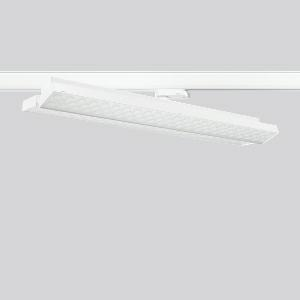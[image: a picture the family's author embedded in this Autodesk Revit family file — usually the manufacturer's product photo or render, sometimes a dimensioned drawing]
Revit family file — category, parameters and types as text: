
# Revit family: tx-move_742163_002_1_76_9c2b
name_source: partatom
category: Lighting Fixtures
units: mm (PartAtom-declared; Revit-internal decimal feet)

## family parameters
Cut with Voids When Loaded = No
Host = Face
Light Source = No
Part Type = Normal
Room Calculation Point = No
Round Connector Dimension = Use Diameter
Shared = No

## types (1)
- MultiLumen 1 (1 x LED Modul 840, 2950 lm, 4000)
    Apparent Load = 41 VA
    CIE Flux Codes = 65 90 98 100 100
    Color Rendering = 80
    Color Temperature = 4000
    Default Elevation = 1800 mm
    Description = Series: TX-MOVE
Multifunctional surface-mounted spotlight for area lighting. Very flat design. Housing: sheet steel, powder-coated. Rotation range: 356°. Swivel range: 90°. Consistent alignment possible with visible tilt scale. High-efficiency LED units with optimum light control thanks to clear plastic (PC) lens optics. Spezielle Mikrostrukturen reduzieren Gelbsaum. Asymmetrical light distribution. With adapter for RZB 3-circuit DALI tracks. Suitable for Track on ceiling. MultiLumen: Luminous flux adjustable in 3 steps. Factory setting is the highest luminous flux. Environmentally friendly and resource-saving due to replaceable and recyclable components. 
Colour: traffic white, matt (RAL 9016)
Length: 570 mm
Width: 119 mm
Height: 88 mm
Lamp: LED
Socket: without socket
Colour temperature: 4000K
Colour rendering index (CRI): 80
System power: 41 W
Rated luminous flux: 5900 lm
Luminous efficiency: 144 lm/W
System power 2: 57 W
Rated luminous flux 2: 8000 lm
Luminous efficiency 2: 140 lm/W
System power 3: 73 W
Rated luminous flux 3: 9750 lm
Luminous efficiency 3: 134 lm/W
Control gear: Dimmable EVG, DALI
Protection class: I
Type of protection: IP 20
    Height = 75 mm
    Lamp = 1 x LED Modul 840
    Lamp Light Flux = 2950 lm
    Lamp count = 1
    Length = 569 mm
    Lifetime = 50000 h
    Luminous efficacy = 144 lm/W
    Manufacturer = RZB
    ModVariant = No
    Model = 742163.002.1.76
    Mounting Place = Ceiling
    Mounting Type = Surface mounted
    Number of Poles = 1
    OnlyDefault = Yes
    Power Factor = 1
    Product Name = TX-MOVE
    Product group = Track mounted projectors
    ProductGroupID = 301
    Protection Class = Protection class I
    Protection Degree = IP 20
    RLX_Detail_Level = 1
    RLX_Emergency_Light_Flux = 0 lm
    RLX_Emergency_Type = 0
    RLX_Emergency_Type_DB = No
    RlxData = <blob elided: 52025 chars, md5=b328e8ea>
    Socket = socket
    Standby Power = 0 W
    System Light Flux = 5900 lm
    System Power = 41 W
    Type Comments = MultiLumen 1
    Type Image = 742162.002.jpg
    URL = http://relux.com
    VarID = multilumen_1
    Voltage = 0 V
    Weight = 0.00 kg
    Width = 119 mm

## geometry (parser evidence)
native form markers: Blend x4, Sweep x16
no freeform markers — native parametric forms only
